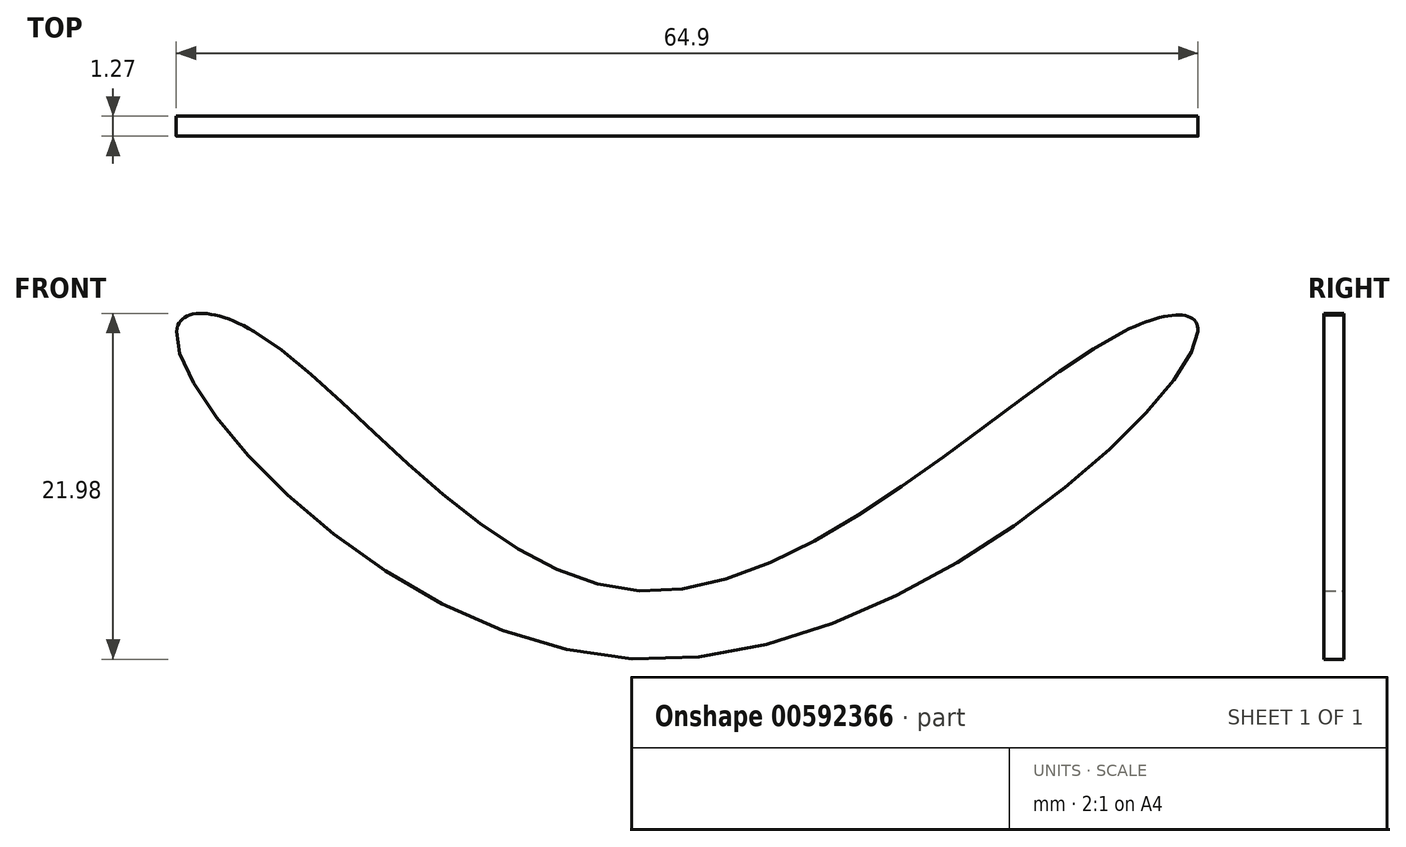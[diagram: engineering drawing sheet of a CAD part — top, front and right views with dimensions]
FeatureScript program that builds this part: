
annotation { "Feature Type Name" : "Feature", "Feature Type Description" : "" }
export const myFeature = defineFeature(function(context is Context, id is Id, definition is map)
    precondition{}
    {
        {
            var Q0;
            Q0=qCreatedBy(makeId("Front.planeOp"),FACE);
            var sketch = newSketch(context, id + "F0", { "sketchPlane" : qUnion([Q0])});
            skFitSpline(sketch, "E0", {"points": [v(-29.5, 0) * mm, v(0, -20.82) * mm, v(35.4, 0) * mm, v(30.7, 0) * mm, v(0, -16.48) * mm, v(-24.57, 0) * mm, v(-29.5, 0) * mm]});
            skLineSegment(sketch, "E1", {"start": v(-29.5, 0) * mm, "end": v(-24.57, 0) * mm});
            skLineSegment(sketch, "E2", {"start": v(35.4, 0) * mm, "end": v(30.7, 0) * mm});
            skSolve(sketch);
        }
        {
            var Q0;
            Q0 = qSketchRegion(id + "F0", true);
            extrude(context, id + "F1", {"entities" : qUnion([Q0]), "depth" : 1.27 * mm, "offsetDistance" : 25.4 * mm});
        }
    });
